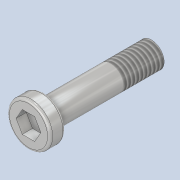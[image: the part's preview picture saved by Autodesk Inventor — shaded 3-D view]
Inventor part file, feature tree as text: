
AUTODESK INVENTOR PART (.ipt)
format: ipt  version: 2020.4 (Build 244396000, 396)  size: 152,064 bytes
history: native  units: mm
features: extrude x4, sketch x4, thread x1, fillet x1, plane x1, projected_geometry x1
ambient origin geometry x8: Origin, YZ Plane, XZ Plane, XY Plane, X Axis, Y Axis, Z Axis, Center Point
bodies: Solid1 (feature_tree)
feature tree (12):
  extrude  "Extrusion1"  Depth=3.0mm TaperAngle=0.0deg
  extrude  "Extrusion2"  Depth=40.0mm TaperAngle=0.0deg
  thread  "Thread1"  [1 undecoded]
  extrude  "Extrusion3"  Depth=2.0mm TaperAngle=0.0deg
  fillet  "Fillet1"  Radius=0.5mm
  plane  "Work Plane1"
  extrude  "Extrusion4"  Depth=0.5mm
  sketch  "Sketch1"  dims[d0=8.45mm d1=3.0mm d2=0.0mm]
  sketch  "Sketch2"  dims[d3=4.95mm d4=40.0mm d5=0.0mm d6=27.0mm d7=0.0mm]
  sketch  "Sketch3"  dims[d8=2.1mm d10=2.0mm d11=0.0mm d12=0.5mm]
  sketch  "Sketch4"  dims[d13=4.2mm d14=15.5mm d15=19.0mm d16=0.0mm d18=9.0mm d19=1.5mm d23=0.5mm d24=0.872665mm d25=0.5mm d26=0.872665mm]
  projected_geometry  "Projected Loop1"
note: 1 required parameter value undecoded (feature->parameter linkage not recoverable at this tier; creation-order binding heuristic only, values carry confidence <= 0.55)
